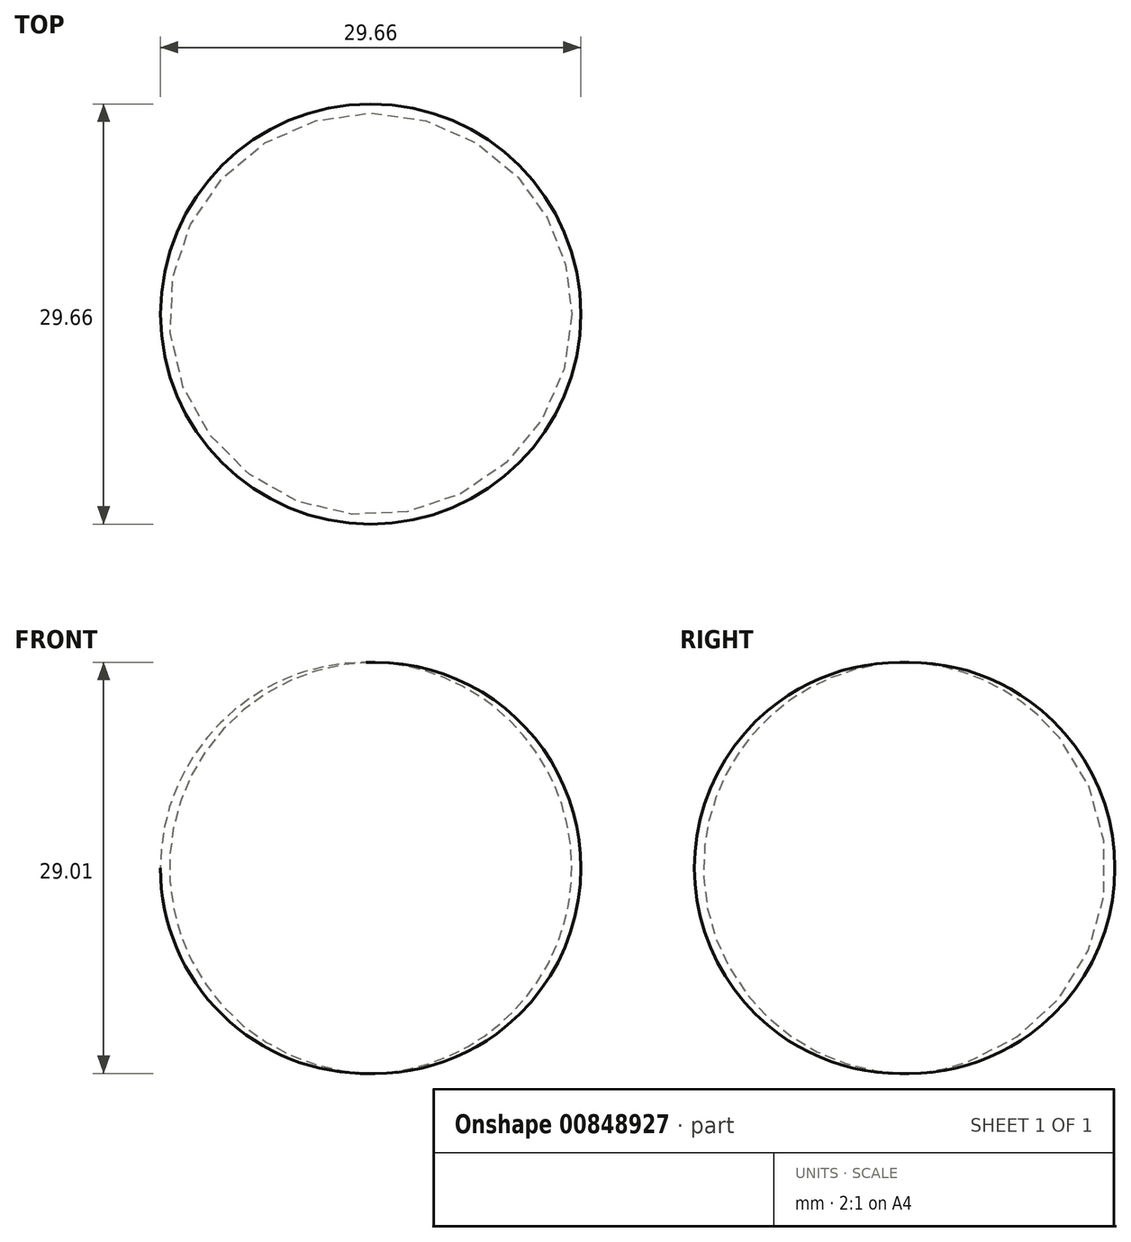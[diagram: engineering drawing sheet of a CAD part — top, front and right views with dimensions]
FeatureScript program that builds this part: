
annotation { "Feature Type Name" : "Feature", "Feature Type Description" : "" }
export const myFeature = defineFeature(function(context is Context, id is Id, definition is map)
    precondition{}
    {
        {
            var Q0;
            Q0=qCreatedBy(makeId("Front.planeOp"),FACE);
            var sketch = newSketch(context, id + "F0", { "sketchPlane" : qUnion([Q0])});
            skArc(sketch, "E0", {"start": v(0, 0) * mm, "mid": v(14.19, 14.5) * mm, "end": v(0, 29.01) * mm});
            skSolve(sketch);
        }
        {
            var Q0;
            Q0=qCreatedBy(makeId("Front.planeOp"),FACE);
            var sketch = newSketch(context, id + "F1", { "sketchPlane" : qUnion([Q0])});
            skLineSegment(sketch, "E1", {"start": v(0, 57.66) * mm, "end": v(0, -28) * mm, "construction": true});
            skSolve(sketch);
        }
        {
            var Q0;
            Q0 = qSketchRegion(id + "F1", true);
            var Q1;
            Q1=sQuery(id+"F0.wireOp",EDGE,"E0");
            var Q2;
            Q2=sQuery(id+"F1.wireOp",EDGE,"E1");
            revolve(context, id + "F2", {"bodyType" : ToolBodyType.SURFACE, "surfaceOperationType" : NewSurfaceOperationType.NEW, "entities" : qUnion([Q0]), "surfaceEntities" : qUnion([Q1]), "axis" : qUnion([Q2]), "revolveType" : RevolveType.FULL});
        }
    });
